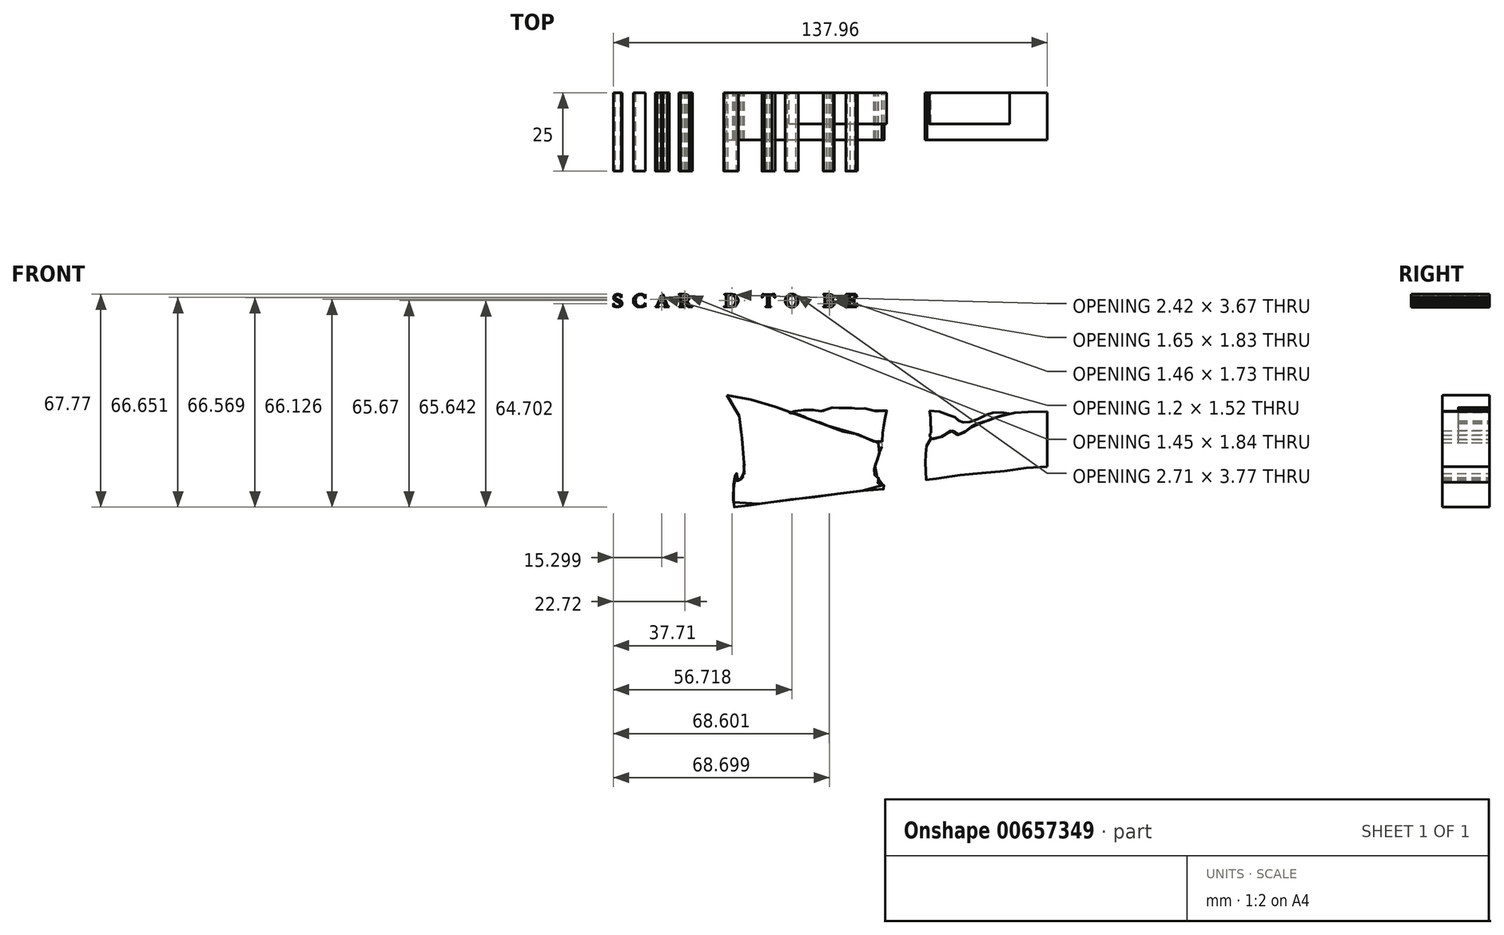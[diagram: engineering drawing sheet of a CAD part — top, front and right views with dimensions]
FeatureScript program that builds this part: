
annotation { "Feature Type Name" : "Feature", "Feature Type Description" : "" }
export const myFeature = defineFeature(function(context is Context, id is Id, definition is map)
    precondition{}
    {
        {
            var Q0;
            Q0=qCreatedBy(makeId("Front.planeOp"),FACE);
            var sketch = newSketch(context, id + "F0", { "sketchPlane" : qUnion([Q0])});
            skFitSpline(sketch, "E0", {"points": [v(-62.93, 10.02) * mm, v(-62.68, 9.62) * mm, v(-62.41, 9.29) * mm, v(-62.08, 9.09) * mm, v(-61.69, 9.04) * mm, v(-61.22, 9.1) * mm, v(-60.88, 9.35) * mm, v(-60.8, 9.67) * mm, v(-60.86, 10.1) * mm, v(-61.2, 10.37) * mm, v(-62, 10.65) * mm, v(-62.48, 10.9) * mm, v(-62.8, 11.26) * mm, v(-62.94, 11.72) * mm, v(-62.86, 12.22) * mm, v(-62.56, 12.68) * mm, v(-62.2, 12.85) * mm, v(-61.75, 12.95) * mm, v(-61.24, 12.95) * mm, v(-60.9, 12.83) * mm, v(-60.66, 12.7) * mm, v(-60.6, 12.7) * mm, v(-60.55, 12.74) * mm, v(-60.51, 12.82) * mm, v(-60.46, 12.92) * mm, v(-60.44, 12.95) * mm], "startDerivative": vector(4, -9.17) * mm, "endDerivative": vector(1.28, 1.5) * mm});
            skLineSegment(sketch, "E1", {"start": v(-60.44, 12.95) * mm, "end": v(-60.44, 11.8) * mm});
            skFitSpline(sketch, "E2", {"points": [v(-60.44, 11.8) * mm, v(-60.5, 11.86) * mm, v(-60.63, 12.12) * mm, v(-60.85, 12.42) * mm, v(-61.13, 12.63) * mm, v(-61.46, 12.75) * mm, v(-61.68, 12.77) * mm, v(-61.93, 12.73) * mm, v(-62.13, 12.62) * mm, v(-62.29, 12.42) * mm, v(-62.4, 12.18) * mm, v(-62.4, 11.88) * mm, v(-62.26, 11.67) * mm, v(-62.1, 11.51) * mm, v(-61.84, 11.4) * mm, v(-61.52, 11.27) * mm, v(-61.28, 11.18) * mm, v(-61, 11.1) * mm, v(-60.76, 11) * mm, v(-60.5, 10.8) * mm, v(-60.33, 10.57) * mm, v(-60.2, 10.2) * mm, v(-60.18, 10.02) * mm, v(-60.24, 9.67) * mm, v(-60.44, 9.28) * mm, v(-60.8, 9) * mm, v(-61.2, 8.87) * mm, v(-61.66, 8.84) * mm, v(-62.1, 8.86) * mm, v(-62.4, 8.94) * mm, v(-62.5, 9.02) * mm, v(-62.59, 9.13) * mm, v(-62.63, 9.14) * mm, v(-62.66, 9.12) * mm, v(-62.76, 9.01) * mm, v(-62.85, 8.9) * mm, v(-62.93, 8.87) * mm], "startDerivative": vector(-3.15, 2.66) * mm, "endDerivative": vector(-3.33, -2.24) * mm});
            skLineSegment(sketch, "E3", {"start": v(-62.93, 8.87) * mm, "end": v(-62.93, 10.02) * mm});
            skFitSpline(sketch, "E4", {"points": [v(-52.77, 11.57) * mm, v(-52.93, 11.73) * mm, v(-53.1, 12.06) * mm, v(-53.33, 12.4) * mm, v(-53.72, 12.66) * mm, v(-54.06, 12.8) * mm, v(-54.35, 12.82) * mm, v(-54.69, 12.77) * mm, v(-55.08, 12.6) * mm, v(-55.36, 12.38) * mm, v(-55.56, 12.15) * mm, v(-55.77, 11.8) * mm, v(-55.89, 11.4) * mm, v(-55.92, 10.95) * mm, v(-55.88, 10.56) * mm, v(-55.8, 10.14) * mm, v(-55.66, 9.8) * mm, v(-55.5, 9.55) * mm, v(-55.23, 9.33) * mm, v(-54.95, 9.17) * mm, v(-54.67, 9.08) * mm, v(-54.3, 9.03) * mm, v(-53.93, 9.12) * mm, v(-53.57, 9.3) * mm, v(-53.2, 9.62) * mm, v(-52.96, 10) * mm, v(-52.84, 10.2) * mm, v(-52.77, 10.22) * mm], "startDerivative": vector(-5.63, 4.7) * mm, "endDerivative": vector(-0.16, 0.67) * mm});
            skLineSegment(sketch, "E5", {"start": v(-52.77, 10.22) * mm, "end": v(-52.77, 8.94) * mm});
            skFitSpline(sketch, "E6", {"points": [v(-52.77, 8.94) * mm, v(-52.89, 8.94) * mm, v(-52.95, 9.03) * mm, v(-53, 9.14) * mm, v(-53.04, 9.18) * mm, v(-53.16, 9.18) * mm, v(-53.24, 9.1) * mm, v(-53.48, 9.02) * mm, v(-53.74, 8.94) * mm, v(-54.06, 8.88) * mm, v(-54.53, 8.86) * mm, v(-55.05, 8.9) * mm, v(-55.49, 9.03) * mm, v(-56.02, 9.33) * mm, v(-56.3, 9.68) * mm, v(-56.55, 10.15) * mm, v(-56.6, 10.5) * mm, v(-56.6, 11.2) * mm, v(-56.46, 11.68) * mm, v(-56.2, 12.16) * mm, v(-55.68, 12.64) * mm, v(-54.96, 12.97) * mm, v(-54.25, 13.02) * mm, v(-53.79, 12.93) * mm, v(-53.42, 12.78) * mm, v(-53.16, 12.63) * mm, v(-53.1, 12.58) * mm, v(-53.06, 12.58) * mm, v(-53.02, 12.59) * mm, v(-52.95, 12.72) * mm, v(-52.87, 12.88) * mm, v(-52.77, 12.93) * mm], "startDerivative": vector(-6.52, -1.15) * mm, "endDerivative": vector(3.69, 0.66) * mm});
            skLineSegment(sketch, "E7", {"start": v(-52.77, 11.57) * mm, "end": v(-52.77, 12.93) * mm});
            skFitSpline(sketch, "E8", {"points": [v(-45.21, 8.96) * mm, v(-45.44, 9.04) * mm, v(-45.7, 9.14) * mm, v(-45.84, 9.4) * mm], "startDerivative": vector(-0.67, 0.29) * mm, "endDerivative": vector(-0.3, 0.87) * mm});
            skLineSegment(sketch, "E9", {"start": v(-45.84, 9.4) * mm, "end": v(-47.2, 12.98) * mm});
            skFitSpline(sketch, "E10", {"points": [v(-47.2, 12.98) * mm, v(-47.3, 12.83) * mm, v(-47.47, 12.66) * mm, v(-47.67, 12.57) * mm, v(-47.71, 12.56) * mm], "startDerivative": vector(-0.35, -0.53) * mm, "endDerivative": vector(-0.29, -0.06) * mm});
            skLineSegment(sketch, "E11", {"start": v(-47.71, 12.56) * mm, "end": v(-49.06, 9.26) * mm});
            skFitSpline(sketch, "E12", {"points": [v(-49.06, 9.26) * mm, v(-49.15, 9.16) * mm, v(-49.3, 9.08) * mm, v(-49.5, 9.02) * mm, v(-49.58, 8.98) * mm, v(-49.6, 8.92) * mm], "startDerivative": vector(-0.35, -0.55) * mm, "endDerivative": vector(-0.1, -0.28) * mm});
            skLineSegment(sketch, "E13", {"start": v(-49.6, 8.92) * mm, "end": v(-48.32, 8.92) * mm});
            skFitSpline(sketch, "E14", {"points": [v(-48.32, 8.92) * mm, v(-48.32, 8.97) * mm, v(-48.47, 9.02) * mm, v(-48.7, 9.12) * mm, v(-48.8, 9.24) * mm, v(-48.7, 9.55) * mm, v(-48.57, 9.82) * mm], "startDerivative": vector(0.19, 0.68) * mm, "endDerivative": vector(0.58, 1.2) * mm});
            skLineSegment(sketch, "E15", {"start": v(-48.57, 9.82) * mm, "end": v(-48.33, 10.4) * mm});
            skLineSegment(sketch, "E16", {"start": v(-47.62, 12.14) * mm, "end": v(-47.04, 10.61) * mm});
            skFitSpline(sketch, "E17", {"points": [v(-46.57, 9.39) * mm, v(-46.53, 9.24) * mm, v(-46.62, 9.14) * mm, v(-46.78, 9.05) * mm, v(-46.92, 9) * mm, v(-46.95, 8.95) * mm, v(-46.95, 8.9) * mm], "startDerivative": vector(0.39, -0.82) * mm, "endDerivative": vector(0.03, -0.5) * mm});
            skLineSegment(sketch, "E18", {"start": v(-46.95, 8.9) * mm, "end": v(-45.2, 8.9) * mm});
            skFitSpline(sketch, "E19", {"points": [v(-45.21, 8.96) * mm, v(-45.2, 8.9) * mm], "startDerivative": vector(0, -0.07) * mm, "endDerivative": vector(0, -0.07) * mm});
            skLineSegment(sketch, "E20", {"start": v(-48.24, 10.61) * mm, "end": v(-47.04, 10.61) * mm});
            skLineSegment(sketch, "E21", {"start": v(-48.33, 10.4) * mm, "end": v(-46.96, 10.4) * mm});
            skLineSegment(sketch, "E22.trimOffspring", {"start": v(-48.24, 10.61) * mm, "end": v(-47.62, 12.14) * mm});
            skLineSegment(sketch, "E23.trimOffspring", {"start": v(-46.96, 10.4) * mm, "end": v(-46.57, 9.39) * mm});
            skLineSegment(sketch, "E24", {"start": v(-41.56, 12.2) * mm, "end": v(-41.56, 9.37) * mm});
            skFitSpline(sketch, "E25", {"points": [v(-41.56, 9.37) * mm, v(-41.6, 9.23) * mm, v(-41.67, 9.16) * mm, v(-41.83, 9.08) * mm, v(-42.06, 9.03) * mm, v(-42.12, 9) * mm, v(-42.12, 8.88) * mm], "startDerivative": vector(-0.12, -0.93) * mm, "endDerivative": vector(0.05, -0.87) * mm});
            skLineSegment(sketch, "E26", {"start": v(-42.12, 8.88) * mm, "end": v(-40.22, 8.88) * mm});
            skFitSpline(sketch, "E27", {"points": [v(-40.22, 8.88) * mm, v(-40.25, 8.95) * mm, v(-40.33, 9) * mm, v(-40.54, 9.01) * mm, v(-40.7, 9.07) * mm, v(-40.84, 9.19) * mm, v(-40.92, 9.34) * mm, v(-40.95, 9.49) * mm], "startDerivative": vector(-0.24, 0.73) * mm, "endDerivative": vector(-0.12, 1.03) * mm});
            skLineSegment(sketch, "E28", {"start": v(-40.95, 9.49) * mm, "end": v(-40.95, 10.69) * mm});
            skLineSegment(sketch, "E29", {"start": v(-40.95, 12.74) * mm, "end": v(-40.3, 12.74) * mm});
            skFitSpline(sketch, "E30", {"points": [v(-40.3, 12.74) * mm, v(-40.1, 12.69) * mm, v(-39.93, 12.61) * mm, v(-39.74, 12.49) * mm, v(-39.61, 12.32) * mm, v(-39.52, 12.13) * mm, v(-39.5, 11.85) * mm, v(-39.52, 11.54) * mm, v(-39.63, 11.33) * mm, v(-39.8, 11.16) * mm, v(-39.98, 11.04) * mm, v(-40.15, 10.98) * mm, v(-40.3, 10.93) * mm, v(-40.55, 10.9) * mm, v(-40.78, 10.9) * mm, v(-40.95, 10.9) * mm], "startDerivative": vector(3.33, -0.7) * mm, "endDerivative": vector(-2.77, 0.04) * mm});
            skFitSpline(sketch, "E31", {"points": [v(-40.95, 10.69) * mm, v(-40.76, 10.69) * mm, v(-40.6, 10.67) * mm, v(-40.4, 10.56) * mm, v(-39.92, 10.01) * mm, v(-39.47, 9.4) * mm, v(-39.15, 8.9) * mm, v(-39.13, 8.9) * mm], "startDerivative": vector(1.73, 0.02) * mm, "endDerivative": vector(0.54, 0.08) * mm});
            skLineSegment(sketch, "E32", {"start": v(-39.13, 8.9) * mm, "end": v(-37.81, 8.9) * mm});
            skFitSpline(sketch, "E33", {"points": [v(-37.81, 8.9) * mm, v(-37.84, 8.97) * mm, v(-37.98, 9.03) * mm, v(-38.18, 9.05) * mm, v(-38.38, 9.21) * mm, v(-38.72, 9.54) * mm], "startDerivative": vector(-0.15, 0.6) * mm, "endDerivative": vector(-1.2, 1.17) * mm});
            skLineSegment(sketch, "E34", {"start": v(-38.72, 9.54) * mm, "end": v(-39.38, 10.47) * mm});
            skFitSpline(sketch, "E35", {"points": [v(-39.38, 10.47) * mm, v(-39.44, 10.56) * mm, v(-39.5, 10.61) * mm, v(-39.6, 10.65) * mm, v(-39.68, 10.66) * mm, v(-39.65, 10.75) * mm, v(-39.38, 10.87) * mm, v(-39.15, 11.05) * mm, v(-38.9, 11.35) * mm, v(-38.78, 11.7) * mm, v(-38.8, 12.12) * mm, v(-39.06, 12.53) * mm, v(-39.38, 12.76) * mm, v(-39.74, 12.9) * mm, v(-40.27, 12.92) * mm, v(-40.97, 12.92) * mm, v(-41.74, 12.92) * mm, v(-42.13, 12.92) * mm, v(-42.13, 12.9) * mm, v(-42.1, 12.82) * mm, v(-41.99, 12.77) * mm, v(-41.86, 12.74) * mm, v(-41.76, 12.71) * mm, v(-41.68, 12.66) * mm, v(-41.61, 12.56) * mm, v(-41.56, 12.41) * mm, v(-41.56, 12.2) * mm], "startDerivative": vector(-2.37, 3.6) * mm, "endDerivative": vector(-0.63, -6.37) * mm});
            skLineSegment(sketch, "E36.trimOffspring", {"start": v(-40.95, 10.9) * mm, "end": v(-40.95, 12.74) * mm});
            skLineSegment(sketch, "E37", {"start": v(-34.77, 8.92) * mm, "end": v(-31.33, 8.92) * mm});
            skLineSegment(sketch, "E38", {"start": v(-31.33, 8.92) * mm, "end": v(-31.06, 9.96) * mm});
            skFitSpline(sketch, "E39", {"points": [v(-31.06, 9.96) * mm, v(-31.12, 10) * mm, v(-31.22, 9.9) * mm, v(-31.39, 9.6) * mm, v(-31.6, 9.38) * mm, v(-31.91, 9.14) * mm, v(-32.3, 9.05) * mm, v(-32.79, 9.01) * mm, v(-33.17, 9.05) * mm, v(-33.42, 9.16) * mm, v(-33.58, 9.36) * mm], "startDerivative": vector(-1.12, 1.19) * mm, "endDerivative": vector(-0.75, 2.58) * mm});
            skLineSegment(sketch, "E40", {"start": v(-33.58, 9.36) * mm, "end": v(-33.58, 10.6) * mm});
            skFitSpline(sketch, "E41", {"points": [v(-33.58, 10.6) * mm, v(-33.56, 10.74) * mm, v(-33.28, 10.83) * mm, v(-32.95, 10.81) * mm, v(-32.65, 10.72) * mm, v(-32.44, 10.52) * mm, v(-32.37, 10.34) * mm, v(-32.3, 10.15) * mm, v(-32.24, 10.05) * mm, v(-32.16, 10.04) * mm], "startDerivative": vector(0.16, 1.52) * mm, "endDerivative": vector(1.26, 0) * mm});
            skLineSegment(sketch, "E42", {"start": v(-32.16, 10.04) * mm, "end": v(-32.16, 11.78) * mm});
            skFitSpline(sketch, "E43", {"points": [v(-32.16, 11.78) * mm, v(-32.22, 11.78) * mm, v(-32.3, 11.63) * mm, v(-32.38, 11.42) * mm, v(-32.55, 11.25) * mm, v(-32.8, 11.11) * mm, v(-33.08, 11.03) * mm, v(-33.46, 11.01) * mm, v(-33.59, 11.03) * mm], "startDerivative": vector(-0.93, 0.25) * mm, "endDerivative": vector(-1.11, 0.17) * mm});
            skLineSegment(sketch, "E44", {"start": v(-33.59, 11.03) * mm, "end": v(-33.59, 12.65) * mm});
            skFitSpline(sketch, "E45", {"points": [v(-33.59, 12.65) * mm, v(-33.53, 12.71) * mm, v(-33.39, 12.78) * mm, v(-33.05, 12.79) * mm, v(-32.64, 12.79) * mm, v(-32.3, 12.74) * mm, v(-32.06, 12.65) * mm, v(-31.75, 12.36) * mm, v(-31.47, 12.07) * mm, v(-31.33, 11.9) * mm, v(-31.29, 11.9) * mm, v(-31.34, 12.12) * mm, v(-31.35, 12.13) * mm], "startDerivative": vector(0.84, 1.27) * mm, "endDerivative": vector(-0.1, 0.17) * mm});
            skLineSegment(sketch, "E46", {"start": v(-31.35, 12.13) * mm, "end": v(-31.65, 12.93) * mm});
            skLineSegment(sketch, "E47", {"start": v(-31.65, 12.93) * mm, "end": v(-34.75, 12.93) * mm});
            skFitSpline(sketch, "E48", {"points": [v(-34.75, 12.93) * mm, v(-34.75, 12.88) * mm, v(-34.64, 12.83) * mm, v(-34.43, 12.77) * mm, v(-34.26, 12.64) * mm, v(-34.22, 12.52) * mm], "startDerivative": vector(-0.1, -0.41) * mm, "endDerivative": vector(0.09, -0.63) * mm});
            skLineSegment(sketch, "E49", {"start": v(-34.22, 12.52) * mm, "end": v(-34.22, 9.39) * mm});
            skFitSpline(sketch, "E50", {"points": [v(-34.22, 9.39) * mm, v(-34.23, 9.26) * mm, v(-34.45, 9.1) * mm, v(-34.7, 9) * mm, v(-34.77, 8.92) * mm], "startDerivative": vector(0.07, -0.64) * mm, "endDerivative": vector(-0.3, -0.4) * mm});
            skSolve(sketch);
        }
        {
            var Q0;
            Q0 = qSketchRegion(id + "F0", true);
            extrude(context, id + "F1", {"entities" : qUnion([Q0]), "depth" : 25 * mm, "offsetDistance" : 25 * mm});
        }
        {
            var Q0;
            Q0=qCreatedBy(makeId("Front.planeOp"),FACE);
            var sketch = newSketch(context, id + "F2", { "sketchPlane" : qUnion([Q0])});
            skLineSegment(sketch, "E51", {"start": v(-27.14, 12.43) * mm, "end": v(-27.14, 9.41) * mm});
            skFitSpline(sketch, "E52", {"points": [v(-27.14, 9.41) * mm, v(-27.14, 9.23) * mm, v(-27.24, 9.16) * mm, v(-27.46, 9.07) * mm, v(-27.8, 8.95) * mm, v(-27.85, 8.95) * mm, v(-27.81, 8.88) * mm, v(-27.73, 8.88) * mm, v(-26.61, 8.88) * mm, v(-25.27, 8.87) * mm, v(-24.54, 9.03) * mm, v(-23.8, 9.41) * mm, v(-23.42, 10.16) * mm, v(-23.25, 10.93) * mm, v(-23.42, 11.72) * mm, v(-23.9, 12.38) * mm, v(-24.74, 12.83) * mm, v(-25.77, 12.92) * mm, v(-26.9, 12.92) * mm, v(-27.64, 12.94) * mm, v(-27.7, 12.9) * mm, v(-27.58, 12.83) * mm, v(-27.34, 12.72) * mm, v(-27.14, 12.43) * mm], "startDerivative": vector(1.22, -7.66) * mm, "endDerivative": vector(4.86, -8.9) * mm});
            skSolve(sketch);
        }
        {
            var Q0;
            Q0 = qSketchRegion(id + "F2", true);
            extrude(context, id + "F3", {"entities" : qUnion([Q0]), "depth" : 25 * mm, "offsetDistance" : 25 * mm});
        }
        {
            var Q0;
            Q0=qCreatedBy(makeId("Front.planeOp"),FACE);
            var sketch = newSketch(context, id + "F4", { "sketchPlane" : qUnion([Q0])});
            skLineSegment(sketch, "E53", {"start": v(-26.44, 12.73) * mm, "end": v(-26.44, 9.4) * mm});
            skFitSpline(sketch, "E54", {"points": [v(-26.44, 9.4) * mm, v(-26.34, 9.2) * mm, v(-26.09, 9.07) * mm, v(-25.64, 9.04) * mm, v(-24.96, 9.2) * mm, v(-24.3, 9.82) * mm, v(-24, 10.9) * mm, v(-24.08, 11.49) * mm, v(-24.33, 12.04) * mm, v(-24.98, 12.58) * mm, v(-25.72, 12.73) * mm, v(-26.44, 12.73) * mm], "startDerivative": vector(0.89, -4) * mm, "endDerivative": vector(-7.18, 0.12) * mm});
            skSolve(sketch);
        }
        {
            var Q0;
            Q0 = qSketchRegion(id + "F4", true);
            extrude(context, id + "F5", {"entities" : qUnion([Q0]), "operationType" : NewBodyOperationType.REMOVE, "depth" : 25 * mm, "offsetDistance" : 25 * mm});
        }
        {
            var Q0;
            Q0=qCreatedBy(makeId("Front.planeOp"),FACE);
            var sketch = newSketch(context, id + "F6", { "sketchPlane" : qUnion([Q0])});
            skLineSegment(sketch, "E55", {"start": v(-14.94, 12.88) * mm, "end": v(-12.5, 12.88) * mm});
            skFitSpline(sketch, "E56", {"points": [v(-14.94, 12.88) * mm, v(-15.23, 12.92) * mm, v(-15.52, 12.97) * mm, v(-15.53, 12.97) * mm, v(-15.58, 12.81) * mm, v(-15.67, 12.26) * mm, v(-15.72, 11.94) * mm, v(-15.7, 11.89) * mm, v(-15.63, 11.9) * mm, v(-15.53, 12.04) * mm, v(-15.4, 12.24) * mm, v(-15.23, 12.46) * mm, v(-15.03, 12.59) * mm, v(-14.8, 12.68) * mm, v(-14.61, 12.7) * mm, v(-14, 12.7) * mm], "startDerivative": vector(-3.4, 0.42) * mm, "endDerivative": vector(6.31, -0.03) * mm});
            skLineSegment(sketch, "E57", {"start": v(-14, 12.7) * mm, "end": v(-14, 9.54) * mm});
            skFitSpline(sketch, "E58", {"points": [v(-14, 9.54) * mm, v(-14.04, 9.35) * mm, v(-14.15, 9.18) * mm, v(-14.34, 9.04) * mm, v(-14.5, 9) * mm, v(-14.58, 8.97) * mm, v(-14.57, 8.92) * mm, v(-14.57, 8.93) * mm], "startDerivative": vector(-0.07, -1.07) * mm, "endDerivative": vector(0.1, 0.19) * mm});
            skLineSegment(sketch, "E59", {"start": v(-14.57, 8.93) * mm, "end": v(-13.1, 8.93) * mm});
            skLineSegment(sketch, "E60", {"start": v(-13.1, 8.93) * mm, "end": v(-12.8, 8.93) * mm});
            skFitSpline(sketch, "E61", {"points": [v(-12.8, 8.93) * mm, v(-12.8, 8.96) * mm, v(-12.89, 8.98) * mm, v(-12.98, 9.02) * mm, v(-13.13, 9.1) * mm, v(-13.24, 9.22) * mm, v(-13.26, 9.54) * mm], "startDerivative": vector(0.06, 0.46) * mm, "endDerivative": vector(0.05, 2.53) * mm});
            skLineSegment(sketch, "E62", {"start": v(-13.26, 9.54) * mm, "end": v(-13.27, 12.64) * mm});
            skLineSegment(sketch, "E63", {"start": v(-13.27, 12.64) * mm, "end": v(-12.3, 12.64) * mm});
            skFitSpline(sketch, "E64", {"points": [v(-12.3, 12.64) * mm, v(-12.06, 12.48) * mm, v(-11.9, 12.24) * mm, v(-11.65, 11.87) * mm, v(-11.6, 11.82) * mm, v(-11.55, 11.84) * mm, v(-11.58, 12.13) * mm, v(-11.68, 12.92) * mm, v(-11.71, 12.95) * mm, v(-12.5, 12.88) * mm], "startDerivative": vector(2.25, -1.35) * mm, "endDerivative": vector(-5.59, -0.64) * mm});
            skSolve(sketch);
        }
        {
            var Q0;
            Q0 = qSketchRegion(id + "F6", true);
            extrude(context, id + "F7", {"entities" : qUnion([Q0]), "depth" : 25 * mm, "offsetDistance" : 25 * mm});
        }
        {
            var Q0;
            Q0=qCreatedBy(makeId("Front.planeOp"),FACE);
            var sketch = newSketch(context, id + "F8", { "sketchPlane" : qUnion([Q0])});
            skFitSpline(sketch, "E65", {"points": [v(-6.27, 13) * mm, v(-6.82, 12.95) * mm, v(-7.48, 12.62) * mm, v(-7.86, 12.24) * mm, v(-8.2, 11.53) * mm, v(-8.32, 10.76) * mm, v(-8.12, 9.96) * mm, v(-7.66, 9.34) * mm, v(-7.05, 8.96) * mm, v(-6.2, 8.8) * mm, v(-5.2, 9.06) * mm, v(-4.43, 9.83) * mm, v(-4.19, 10.85) * mm, v(-4.35, 11.84) * mm, v(-5.22, 12.78) * mm, v(-6.27, 13) * mm]});
            skSolve(sketch);
        }
        {
            var Q0;
            Q0=qCreatedBy(makeId("Front.planeOp"),FACE);
            var sketch = newSketch(context, id + "F9", { "sketchPlane" : qUnion([Q0])});
            skFitSpline(sketch, "E66", {"points": [v(-6.28, 12.8) * mm, v(-6.62, 12.74) * mm, v(-6.96, 12.5) * mm, v(-7.26, 12.17) * mm, v(-7.48, 11.63) * mm, v(-7.58, 11.05) * mm, v(-7.5, 10.38) * mm, v(-7.36, 9.85) * mm, v(-7.12, 9.45) * mm, v(-6.87, 9.23) * mm, v(-6.53, 9.07) * mm, v(-6.2, 9.01) * mm, v(-5.75, 9.11) * mm, v(-5.27, 9.5) * mm, v(-4.96, 10.18) * mm, v(-4.87, 10.85) * mm, v(-4.94, 11.55) * mm, v(-5.27, 12.2) * mm, v(-5.62, 12.6) * mm, v(-5.98, 12.78) * mm, v(-6.28, 12.8) * mm]});
            skSolve(sketch);
        }
        {
            var Q0;
            Q0 = qSketchRegion(id + "F8", true);
            extrude(context, id + "F10", {"entities" : qUnion([Q0]), "depth" : 25 * mm, "offsetDistance" : 25 * mm});
        }
        {
            var Q0;
            Q0 = qSketchRegion(id + "F9", true);
            extrude(context, id + "F11", {"entities" : qUnion([Q0]), "operationType" : NewBodyOperationType.REMOVE, "depth" : 25 * mm, "offsetDistance" : 25 * mm});
        }
        {
            var Q0;
            Q0=qCreatedBy(makeId("Front.planeOp"),FACE);
            var sketch = newSketch(context, id + "F12", { "sketchPlane" : qUnion([Q0])});
            skLineSegment(sketch, "E67", {"start": v(4.24, 12.34) * mm, "end": v(4.24, 9.48) * mm});
            skFitSpline(sketch, "E68", {"points": [v(4.24, 9.48) * mm, v(4.2, 9.3) * mm, v(4.08, 9.14) * mm, v(3.84, 9.04) * mm, v(3.73, 8.99) * mm, v(3.77, 8.92) * mm, v(3.88, 8.9) * mm], "startDerivative": vector(-0.2, -1) * mm, "endDerivative": vector(0.87, -0.06) * mm});
            skLineSegment(sketch, "E69", {"start": v(3.88, 8.9) * mm, "end": v(6.18, 8.9) * mm});
            skFitSpline(sketch, "E70", {"points": [v(6.18, 8.9) * mm, v(6.45, 8.96) * mm, v(6.8, 9.14) * mm, v(7.07, 9.36) * mm, v(7.26, 9.79) * mm, v(7.22, 10.25) * mm, v(7.03, 10.6) * mm, v(6.68, 10.87) * mm, v(6.33, 10.97) * mm, v(6.32, 10.97) * mm, v(6.33, 10.99) * mm, v(6.63, 11.15) * mm, v(6.9, 11.4) * mm, v(7.06, 11.75) * mm, v(7.04, 12.06) * mm, v(6.95, 12.37) * mm, v(6.64, 12.63) * mm, v(6.25, 12.8) * mm, v(5.71, 12.91) * mm, v(5.22, 12.92) * mm], "startDerivative": vector(5.53, 0.8) * mm, "endDerivative": vector(-7.51, -0.07) * mm});
            skLineSegment(sketch, "E71", {"start": v(5.22, 12.92) * mm, "end": v(3.9, 12.92) * mm});
            skFitSpline(sketch, "E72", {"points": [v(3.9, 12.92) * mm, v(3.83, 12.92) * mm, v(3.8, 12.9) * mm, v(3.86, 12.8) * mm, v(4.08, 12.69) * mm, v(4.22, 12.6) * mm, v(4.24, 12.34) * mm], "startDerivative": vector(-0.64, 0.06) * mm, "endDerivative": vector(-0.1, -1.28) * mm});
            skSolve(sketch);
        }
        {
            var Q0;
            Q0 = qSketchRegion(id + "F12", true);
            extrude(context, id + "F13", {"entities" : qUnion([Q0]), "depth" : 25 * mm, "offsetDistance" : 25 * mm});
        }
        {
            var Q0;
            Q0=qCreatedBy(makeId("Front.planeOp"),FACE);
            var sketch = newSketch(context, id + "F14", { "sketchPlane" : qUnion([Q0])});
            skLineSegment(sketch, "E73", {"start": v(4.93, 12.62) * mm, "end": v(4.93, 11.04) * mm});
            skLineSegment(sketch, "E74", {"start": v(4.93, 11.04) * mm, "end": v(5.65, 11.04) * mm});
            skFitSpline(sketch, "E75", {"points": [v(5.65, 11.04) * mm, v(5.83, 11.07) * mm, v(6.15, 11.29) * mm, v(6.34, 11.6) * mm, v(6.39, 11.87) * mm, v(6.37, 12.1) * mm, v(6.24, 12.37) * mm, v(6.05, 12.56) * mm, v(5.82, 12.68) * mm, v(5.5, 12.75) * mm, v(5.14, 12.77) * mm, v(4.98, 12.75) * mm, v(4.94, 12.7) * mm, v(4.93, 12.62) * mm], "startDerivative": vector(2.68, 0.48) * mm, "endDerivative": vector(-0.28, -1.52) * mm});
            skLineSegment(sketch, "E76", {"start": v(4.93, 10.87) * mm, "end": v(5.65, 10.87) * mm});
            skLineSegment(sketch, "E77", {"start": v(5.65, 10.87) * mm, "end": v(4.93, 10.87) * mm});
            skLineSegment(sketch, "E78", {"start": v(4.93, 10.87) * mm, "end": v(4.93, 9.44) * mm});
            skFitSpline(sketch, "E79", {"points": [v(5.65, 10.87) * mm, v(5.92, 10.8) * mm, v(6.07, 10.72) * mm, v(6.23, 10.6) * mm, v(6.37, 10.48) * mm, v(6.5, 10.28) * mm, v(6.57, 10.09) * mm, v(6.59, 9.87) * mm, v(6.54, 9.7) * mm, v(6.44, 9.49) * mm, v(6.26, 9.25) * mm, v(6.03, 9.13) * mm, v(5.76, 9.05) * mm, v(5.45, 9.02) * mm, v(5.17, 9.07) * mm, v(5.03, 9.15) * mm, v(4.93, 9.44) * mm], "startDerivative": vector(5.44, -0.78) * mm, "endDerivative": vector(-0.65, 6.48) * mm});
            skSolve(sketch);
        }
        {
            var Q0;
            Q0 = qSketchRegion(id + "F14", true);
            extrude(context, id + "F15", {"entities" : qUnion([Q0]), "operationType" : NewBodyOperationType.REMOVE, "depth" : 25 * mm, "offsetDistance" : 25 * mm});
        }
        {
            var Q0;
            Q0=qCreatedBy(makeId("Front.planeOp"),FACE);
            var sketch = newSketch(context, id + "F16", { "sketchPlane" : qUnion([Q0])});
            skLineSegment(sketch, "E80", {"start": v(11.02, 12.93) * mm, "end": v(14.08, 12.93) * mm});
            skLineSegment(sketch, "E81", {"start": v(14.08, 12.93) * mm, "end": v(14.5, 11.98) * mm});
            skLineSegment(sketch, "E82", {"start": v(11.51, 12.35) * mm, "end": v(11.51, 9.42) * mm});
            skLineSegment(sketch, "E83", {"start": v(11.01, 8.88) * mm, "end": v(14.38, 8.88) * mm});
            skLineSegment(sketch, "E84", {"start": v(14.38, 8.88) * mm, "end": v(14.64, 9.82) * mm});
            skFitSpline(sketch, "E85", {"points": [v(11.02, 12.93) * mm, v(11, 12.9) * mm, v(11.01, 12.86) * mm, v(11.07, 12.82) * mm, v(11.21, 12.75) * mm, v(11.39, 12.64) * mm, v(11.48, 12.55) * mm, v(11.51, 12.44) * mm, v(11.51, 12.35) * mm], "startDerivative": vector(-1.03, -0.3) * mm, "endDerivative": vector(0, -0.74) * mm});
            skFitSpline(sketch, "E86", {"points": [v(11.01, 8.88) * mm, v(10.98, 8.88) * mm, v(10.96, 8.9) * mm, v(10.96, 8.96) * mm, v(11.01, 8.99) * mm, v(11.14, 9.03) * mm, v(11.3, 9.1) * mm, v(11.42, 9.2) * mm, v(11.48, 9.29) * mm, v(11.51, 9.37) * mm, v(11.51, 9.42) * mm], "startDerivative": vector(-0.57, -0.08) * mm, "endDerivative": vector(0.22, 0.52) * mm});
            skPoint(sketch, "E87.37.internal.snap0", {"position": v(12.7, 8.88) * mm});
            skPoint(sketch, "E87.47.internal.snap0", {"position": v(12.7, 8.88) * mm});
            skFitSpline(sketch, "E87", {"points": [v(14.5, 11.98) * mm, v(14.5, 11.92) * mm, v(14.42, 11.88) * mm, v(14.32, 11.98) * mm, v(14.23, 12.1) * mm, v(14.04, 12.26) * mm, v(13.85, 12.44) * mm, v(13.66, 12.59) * mm, v(13.44, 12.64) * mm, v(13.11, 12.69) * mm, v(12.77, 12.7) * mm, v(12.36, 12.66) * mm, v(12.24, 12.61) * mm, v(12.23, 12.45) * mm, v(12.24, 12.17) * mm, v(12.24, 11.44) * mm, v(12.22, 11.08) * mm, v(12.22, 11.03) * mm, v(12.23, 11.02) * mm, v(12.28, 11.01) * mm, v(12.63, 11.03) * mm, v(12.92, 11.1) * mm, v(13.21, 11.25) * mm, v(13.37, 11.55) * mm, v(13.5, 11.82) * mm, v(13.54, 11.85) * mm, v(13.57, 11.83) * mm, v(13.6, 11.75) * mm, v(13.6, 11.3) * mm, v(13.6, 10.57) * mm, v(13.6, 10.14) * mm, v(13.57, 10.08) * mm, v(13.53, 10.07) * mm, v(13.46, 10.1) * mm, v(13.4, 10.32) * mm, v(13.17, 10.67) * mm, v(12.89, 10.8) * mm, v(12.7, 10.85) * mm, v(12.41, 10.86) * mm, v(12.24, 10.82) * mm, v(12.21, 10.7) * mm, v(12.2, 10.53) * mm, v(12.22, 10.08) * mm, v(12.23, 9.62) * mm, v(12.26, 9.3) * mm, v(12.3, 9.17) * mm, v(12.48, 9.1) * mm, v(12.7, 9.07) * mm, v(12.97, 9.06) * mm, v(13.36, 9.07) * mm, v(13.78, 9.2) * mm, v(14.19, 9.46) * mm, v(14.4, 9.8) * mm, v(14.55, 10.03) * mm, v(14.62, 10.03) * mm, v(14.64, 9.98) * mm, v(14.64, 9.82) * mm], "startDerivative": vector(1.66, -6.74) * mm, "endDerivative": vector(-3.21, -17.35) * mm});
            skSolve(sketch);
        }
        {
            var Q0;
            Q0 = qSketchRegion(id + "F16", true);
            extrude(context, id + "F17", {"entities" : qUnion([Q0]), "depth" : 25 * mm, "offsetDistance" : 25 * mm});
        }
        {
            var Q0;
            Q0=qCreatedBy(makeId("Front.planeOp"),FACE);
            var sketch = newSketch(context, id + "F18", { "sketchPlane" : qUnion([Q0])});
            skFitSpline(sketch, "E88", {"points": [v(-7.13, -24.7) * mm, v(-6.43, -24.41) * mm, v(-5.36, -24.23) * mm, v(-3.64, -24) * mm, v(-2.2, -23.8) * mm, v(-0.48, -23.85) * mm, v(1.85, -23.85) * mm, v(2.73, -24.13) * mm, v(3.52, -24.41) * mm, v(3.84, -24.27) * mm, v(4.17, -23.95) * mm, v(5.1, -23.39) * mm, v(6.3, -23.16) * mm, v(7.98, -23.16) * mm, v(8.54, -23.25) * mm, v(9.38, -23.3) * mm, v(10.4, -23.3) * mm, v(11.15, -23.25) * mm, v(12.12, -23.16) * mm, v(13.1, -23.2) * mm, v(14.07, -23.39) * mm, v(14.17, -23.39) * mm, v(14.82, -23.48) * mm, v(15.56, -23.3) * mm, v(17.33, -23.44) * mm, v(19.52, -23.85) * mm, v(21.28, -24.64) * mm, v(22.07, -24.18) * mm, v(22.72, -24.13) * mm, v(23.75, -24.13) * mm, v(23.95, -24.08) * mm, v(23.65, -25.58) * mm, v(23.33, -26.62) * mm, v(23.14, -27.92) * mm, v(23.02, -28.8) * mm, v(22.76, -30.26) * mm, v(22.65, -31.7) * mm, v(22.5, -33.3) * mm, v(22.46, -34.13) * mm, v(20.33, -34) * mm, v(14.1, -31.34) * mm, v(9.64, -30.56) * mm, v(6.2, -29.24) * mm, v(2.62, -27.81) * mm, v(-1.79, -26.24) * mm, v(-5.02, -25.07) * mm, v(-7.13, -24.7) * mm]});
            skFitSpline(sketch, "E89", {"points": [v(37.57, -24.1) * mm, v(39.72, -24.24) * mm, v(41.92, -24.7) * mm, v(44.26, -25.75) * mm, v(45, -26.03) * mm, v(45.73, -26.12) * mm, v(46.05, -26.71) * mm, v(46.6, -27.26) * mm, v(47.37, -27.26) * mm, v(48.02, -27.5) * mm, v(48.24, -27.72) * mm, v(48.98, -27.81) * mm, v(49.9, -27.81) * mm, v(51.5, -27.3) * mm, v(53, -26.76) * mm, v(55.25, -25.66) * mm, v(56.17, -25.06) * mm, v(57.36, -24.83) * mm, v(58.83, -24.51) * mm, v(60.52, -24.65) * mm, v(62.08, -24.83) * mm, v(63, -25.16) * mm, v(60.98, -25.52) * mm, v(59.6, -25.98) * mm, v(58.37, -26.35) * mm, v(57.6, -26.44) * mm, v(56.77, -26.94) * mm, v(55.94, -27.26) * mm, v(54.98, -27.4) * mm, v(54.3, -27.9) * mm, v(53.6, -28.22) * mm, v(52.83, -28.22) * mm, v(51.5, -28.5) * mm, v(50.76, -29.28) * mm, v(49.44, -30.15) * mm, v(48.43, -31.16) * mm, v(46.96, -31.52) * mm, v(46.46, -31.7) * mm, v(45.59, -30.97) * mm, v(44.53, -30.33) * mm, v(43.25, -31.2) * mm, v(42.2, -31.89) * mm, v(41.05, -32.44) * mm, v(39.86, -32.76) * mm, v(38.35, -33.22) * mm, v(37.85, -33.22) * mm, v(37.79, -33.2) * mm, v(37.94, -32.88) * mm, v(37.9, -32.6) * mm, v(37.71, -32.23) * mm, v(37.54, -32.03) * mm, v(37.57, -31.9) * mm, v(37.87, -31.34) * mm, v(38.06, -30.7) * mm, v(38.02, -30.04) * mm, v(37.97, -29.02) * mm, v(37.84, -27.84) * mm, v(37.92, -26.88) * mm, v(37.84, -25.85) * mm, v(37.7, -24.85) * mm, v(37.6, -24.36) * mm, v(37.57, -24.1) * mm]});
            skSolve(sketch);
        }
        {
            var Q0;
            Q0 = qSketchRegion(id + "F18", true);
            extrude(context, id + "F19", {"entities" : qUnion([Q0]), "depth" : 10 * mm, "offsetDistance" : 25 * mm});
        }
        {
            var Q0;
            Q0=qCreatedBy(makeId("Front.planeOp"),FACE);
            var sketch = newSketch(context, id + "F20", { "sketchPlane" : qUnion([Q0])});
            skFitSpline(sketch, "E90", {"points": [v(-26.85, -19.2) * mm, v(-25.71, -19.2) * mm, v(-23.8, -19.59) * mm, v(-21.58, -19.98) * mm, v(-19.36, -20.57) * mm, v(-16.2, -21.46) * mm, v(-14.04, -22.3) * mm, v(-12.8, -22.64) * mm, v(-11.67, -22.84) * mm, v(-9.75, -23.33) * mm, v(-8.27, -24.07) * mm, v(-7.78, -24.52) * mm, v(-7.14, -24.76) * mm, v(-4.68, -25.2) * mm, v(-2.28, -26.07) * mm, v(0.83, -27.14) * mm, v(6.2, -29.34) * mm, v(9.03, -30.48) * mm, v(11.35, -30.92) * mm, v(13.4, -31.26) * mm, v(15.33, -31.93) * mm, v(17.7, -32.96) * mm, v(20.03, -34) * mm, v(21.1, -34.33) * mm, v(22.43, -34.33) * mm, v(22.43, -34.36) * mm, v(22.43, -34.76) * mm, v(22.37, -35.46) * mm, v(22.33, -35.73) * mm, v(22.13, -35.9) * mm, v(21.72, -36.84) * mm, v(21.58, -37.63) * mm, v(21.24, -38.4) * mm, v(21, -39.49) * mm, v(20.8, -39.96) * mm, v(20.5, -40.41) * mm, v(20.43, -40.91) * mm, v(20.4, -41.25) * mm, v(20.27, -41.77) * mm, v(20.27, -41.93) * mm, v(20.16, -42.15) * mm, v(19.93, -42.6) * mm, v(19.86, -42.92) * mm, v(19.9, -43.28) * mm, v(20.05, -44.17) * mm, v(20.2, -44.74) * mm, v(20.56, -45) * mm, v(21.27, -45.43) * mm, v(21.4, -45.49) * mm, v(21.39, -45.63) * mm, v(21.27, -46.11) * mm, v(21.1, -46.68) * mm, v(21.1, -47.02) * mm, v(21.27, -47.22) * mm, v(21.83, -47.4) * mm, v(22.78, -47.7) * mm, v(23.16, -47.87) * mm, v(23.18, -48.09) * mm, v(23.2, -48.45) * mm, v(23.18, -48.73) * mm, v(23.1, -48.96) * mm, v(17.82, -49.45) * mm, v(6.94, -50.77) * mm, v(-1.3, -51.74) * mm, v(-10.67, -52.82) * mm, v(-17.84, -53.9) * mm, v(-22.81, -54.54) * mm, v(-24.58, -54.74) * mm, v(-24.6, -54.73) * mm, v(-24.64, -54.53) * mm, v(-24.78, -52.7) * mm, v(-24.88, -52.08) * mm, v(-25, -51.54) * mm, v(-25, -51.19) * mm, v(-24.88, -50.5) * mm, v(-24.87, -49.71) * mm, v(-24.83, -49.27) * mm, v(-24.74, -49.18) * mm, v(-24.7, -48.98) * mm, v(-24.69, -48.54) * mm, v(-24.76, -48.4) * mm, v(-24.72, -47.93) * mm, v(-24.65, -47.27) * mm, v(-24.56, -45.9) * mm, v(-24.44, -45.53) * mm, v(-24.26, -44.9) * mm, v(-24.18, -44.53) * mm, v(-24.2, -44.09) * mm, v(-24.2, -44.07) * mm, v(-24.05, -44.03) * mm, v(-23.74, -44) * mm, v(-23.74, -44.1) * mm, v(-23.79, -44.56) * mm, v(-23.79, -45.01) * mm, v(-23.62, -45.3) * mm, v(-23.59, -45.34) * mm, v(-23.6, -45.35) * mm, v(-23.78, -45.43) * mm, v(-23.92, -45.54) * mm, v(-23.95, -45.67) * mm, v(-23.92, -45.83) * mm, v(-24.03, -45.85) * mm, v(-24.18, -45.9) * mm, v(-24.28, -46) * mm, v(-24.3, -46.1) * mm, v(-24.29, -46.23) * mm, v(-24.27, -46.33) * mm, v(-24.15, -46.35) * mm, v(-23.86, -46.35) * mm, v(-23.4, -46.35) * mm, v(-22.66, -46.04) * mm, v(-22.34, -45.9) * mm, v(-22.12, -45.57) * mm, v(-21.97, -45.32) * mm, v(-21.77, -45.34) * mm, v(-21.72, -45.2) * mm, v(-21.79, -45.05) * mm, v(-21.81, -44.97) * mm, v(-21.7, -44.67) * mm, v(-21.51, -44.47) * mm, v(-21.31, -44.1) * mm, v(-21.36, -43.87) * mm, v(-21.5, -43.6) * mm, v(-21.5, -43.57) * mm, v(-21.38, -43.53) * mm, v(-21.3, -43.46) * mm, v(-21.37, -43.14) * mm, v(-21.4, -42.6) * mm, v(-21.46, -41.95) * mm, v(-21.5, -41.63) * mm, v(-21.4, -41.56) * mm, v(-21.3, -41.48) * mm, v(-21.35, -41.08) * mm, v(-21.43, -40.24) * mm, v(-21.65, -39.26) * mm, v(-21.68, -36.98) * mm, v(-21.92, -34.04) * mm, v(-22.29, -31.8) * mm, v(-22.7, -29.55) * mm, v(-22.54, -28.3) * mm, v(-22.51, -27) * mm, v(-23.06, -25.56) * mm, v(-24.44, -23.4) * mm, v(-25.34, -20.85) * mm, v(-26.3, -19.6) * mm, v(-26.85, -19.2) * mm]});
            skFitSpline(sketch, "E91", {"points": [v(74.99, -24.31) * mm, v(71.1, -24.26) * mm, v(67.15, -24.51) * mm, v(65.65, -24.45) * mm, v(64.52, -24.76) * mm, v(63.77, -24.89) * mm, v(63.15, -25.26) * mm, v(60.79, -25.56) * mm, v(59.43, -26.13) * mm, v(58.25, -26.44) * mm, v(57.72, -26.48) * mm, v(57.24, -26.8) * mm, v(56.32, -27.23) * mm, v(55.4, -27.5) * mm, v(54.78, -27.62) * mm, v(54.21, -28.06) * mm, v(53.56, -28.28) * mm, v(52.64, -28.32) * mm, v(51.63, -28.59) * mm, v(51.06, -29.16) * mm, v(50.49, -29.55) * mm, v(49.88, -29.9) * mm, v(49.26, -30.47) * mm, v(48.82, -30.9) * mm, v(48.25, -31.4) * mm, v(47.38, -31.52) * mm, v(46.76, -31.7) * mm, v(46.41, -31.83) * mm, v(45.8, -31.35) * mm, v(45.01, -30.56) * mm, v(44.57, -30.43) * mm, v(44.05, -30.6) * mm, v(43.26, -31.35) * mm, v(41.77, -32.18) * mm, v(40.32, -32.75) * mm, v(38.61, -33.19) * mm, v(37.82, -33.23) * mm, v(36.88, -34.34) * mm, v(36.7, -34.59) * mm, v(36.67, -34.94) * mm, v(36.67, -35.32) * mm, v(36.45, -35.73) * mm, v(36.32, -35.86) * mm, v(36.4, -36.19) * mm, v(36.34, -37.86) * mm, v(36.28, -38.54) * mm, v(36.38, -39.7) * mm, v(36.3, -40.58) * mm, v(36.14, -41.02) * mm, v(36.34, -41.67) * mm, v(36.34, -42.35) * mm, v(36.34, -43.78) * mm, v(36.34, -44.66) * mm, v(36.51, -45.1) * mm, v(36.48, -45.95) * mm, v(36.3, -46.77) * mm, v(37.38, -46.32) * mm, v(42.67, -45.28) * mm, v(48.72, -44.4) * mm, v(53.96, -43.96) * mm, v(59.27, -43.51) * mm, v(65.4, -42.7) * mm, v(70.75, -42.07) * mm, v(75.02, -41.9) * mm, v(75.02, -41.9) * mm], "startDerivative": vector(-131.01, 9.84) * mm, "endDerivative": vector(-6.16, 2.58) * mm});
            skLineSegment(sketch, "E92", {"start": v(75.02, -41.9) * mm, "end": v(74.99, -24.31) * mm});
            skSolve(sketch);
        }
        {
            var Q0;
            Q0 = qSketchRegion(id + "F20", true);
            extrude(context, id + "F21", {"entities" : qUnion([Q0]), "depth" : 15 * mm, "offsetDistance" : 25 * mm});
        }
    });
